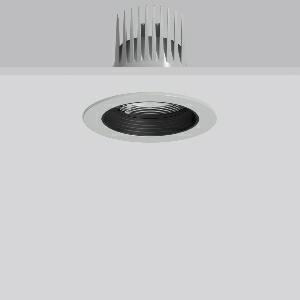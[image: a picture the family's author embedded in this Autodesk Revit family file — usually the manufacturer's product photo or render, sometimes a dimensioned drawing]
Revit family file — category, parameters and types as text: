
# Revit family: heledon_maxi_e_901769_004_25fc
name_source: partatom
category: Lighting Fixtures
units: mm (PartAtom-declared; Revit-internal decimal feet)

## family parameters
Cut with Voids When Loaded = No
Host = Face
Light Source = No
Part Type = Normal
Room Calculation Point = No
Round Connector Dimension = Use Diameter
Shared = No

## types (1)
- HELEDON maxi E (1 x LED Modul 930, 3600 lm, 3000)
    Apparent Load = 35 VA
    Approval mark = CE
    CIE Flux Codes = 96 100 100 100 100
    Color Rendering = 90
    Color Temperature = 3000
    Default Elevation = 1800 mm
    Description = Series: HELEDON maxi
Round recessed downlight. Housing: die-cast aluminium, powder-coated. Black plastic ring and recessed LED to prevent glare from the side. Optical assembly with lens made of plastic (polycarbonate) for the best homogeneous light distribution - can be changed without tools. Best colour rendering index Ra>90. Suitable for Recessed ceiling mounting. Installation without tools thanks to spring fastening system. Including separate LED converter with connecting cable 600 mm.High quality converter without flickering and stroboscopic effect. Through-wiring box (5 pole) available as accessory. The following accessories can be mounted without use of tools: interchangeable lenses, decorative glasses, honeycomb louvre, clear and frosted diffusers, white interchangeable plastic ring. 
Colour: silver
Diameter: 162 mm
Height: 3 mm
Cut-out diameter: 152 mm
Recess height: 200 mm
Luminaire: recess height: 135 mm
Lamp: LED
Socket: without socket
Colour temperature: 3000K
Colour rendering index (CRI): 92
System power: 35 W
Rated luminous flux: 3600 lm
Luminous efficiency: 103 lm/W
Control gear: Regulated power supply
Protection class: II
Type of protection: IP 20
    Height = 0 mm  [stored 0 ft]
    Lamp = 1 x LED Modul 930
    Lamp Light Flux = 3600 lm
    Lamp count = 1
    Length = 162 mm
    Lifetime = 50000 h
    Luminous efficacy = 103 lm/W
    Manufacturer = RZB
    ModVariant = No
    Model = 901769.004
    Mounting Place = Ceiling
    Mounting Type = Recessed
    Number of Poles = 1
    OnlyDefault = Yes
    Power Factor = 1
    Product Name = HELEDON maxi E
    Product group = Recessed downlights
    ProductGroupID = 402
    Protection Class = Protection class II
    Protection Degree = IP 20
    RLX_Detail_Level = 1
    RLX_Emergency_Light_Flux = 0 lm
    RLX_Emergency_Type = 0
    RLX_Emergency_Type_DB = No
    RlxData = <blob elided: 119349 chars, md5=52f85bfd>
    Socket = socket
    Standby Power = 0 W
    System Light Flux = 3600 lm
    System Power = 35 W
    Type Comments = Product without accessories
    Type Image = 901663.004.jpg
    URL = http://relux.com
    VarID = ---
    Voltage = 230 V
    Voltage Range = 220-240 V
    Weight = 0.00 kg
    Width = 0 mm  [stored 0 ft]

note: [stored X ft] marks values corroborated as IEEE doubles in the binary element streams (Revit-internal decimal feet)

## geometry (parser evidence)
native form markers: Blend x4, Sweep x10
no freeform markers — native parametric forms only
